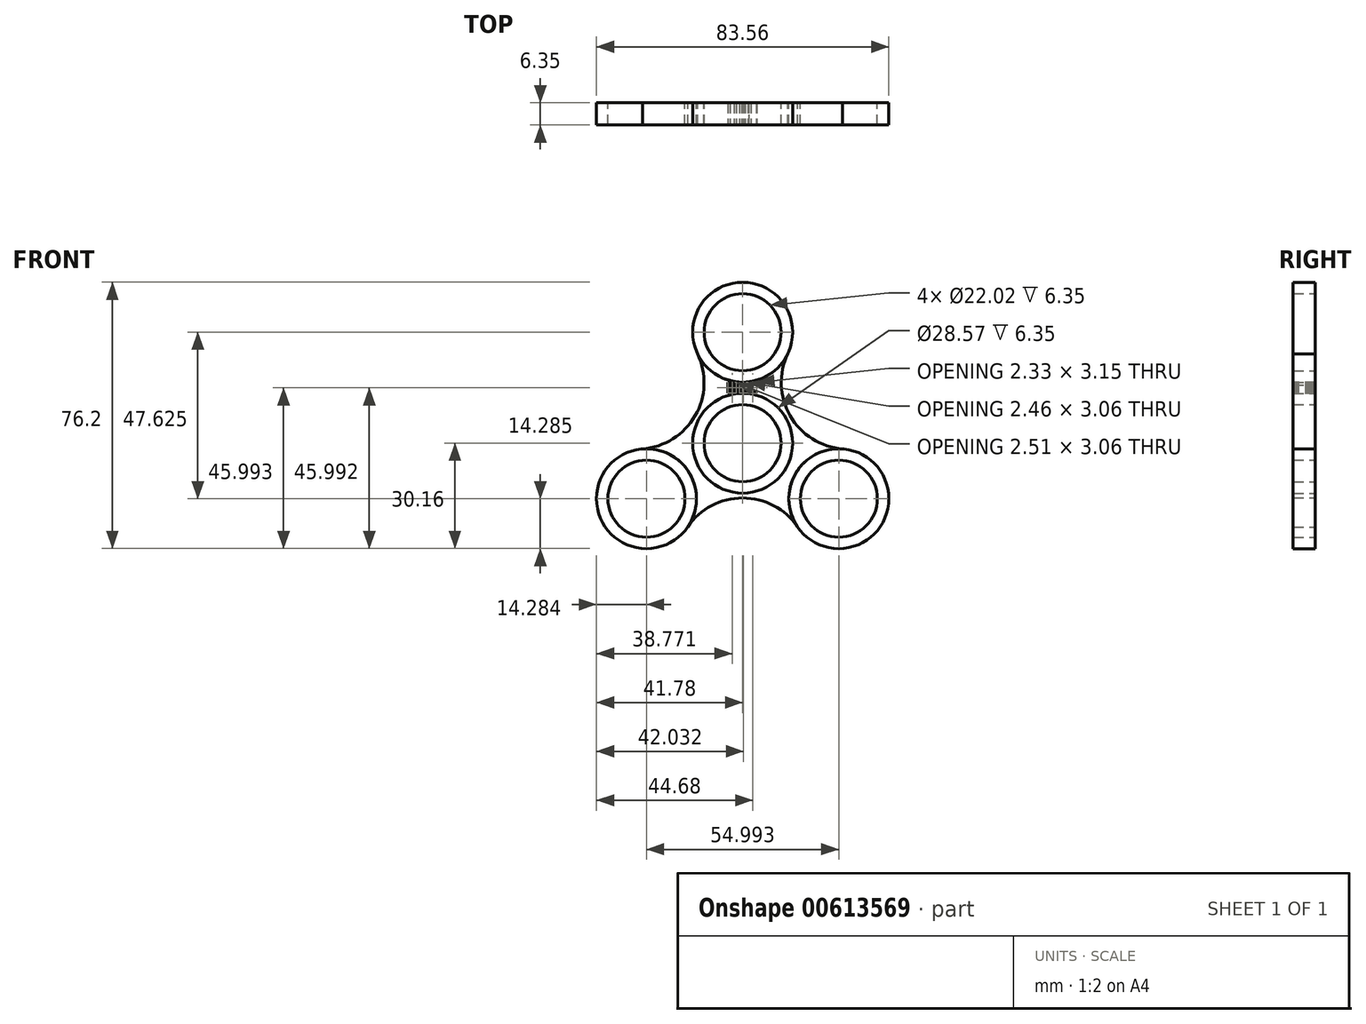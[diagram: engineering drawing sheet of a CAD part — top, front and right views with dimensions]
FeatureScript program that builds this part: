
annotation { "Feature Type Name" : "Feature", "Feature Type Description" : "" }
export const myFeature = defineFeature(function(context is Context, id is Id, definition is map)
    precondition{}
    {
        {
            var Q0;
            Q0=qCreatedBy(makeId("Front.planeOp"),FACE);
            var sketch = newSketch(context, id + "F0", { "sketchPlane" : qUnion([Q0])});
            skCircle(sketch, "E0", {"center": v(0, 0) * mm, "radius": 14.29 * mm});
            skCircle(sketch, "E1", {"center": v(0, 0) * mm, "radius": 11.01 * mm});
            skCircle(sketch, "E2", {"center": v(0, 31.75) * mm, "radius": 14.29 * mm});
            skCircle(sketch, "E3", {"center": v(0, 31.75) * mm, "radius": 11.01 * mm});
            skCircle(sketch, "E4.1.0", {"center": v(-27.5, -15.88) * mm, "radius": 14.29 * mm});
            skCircle(sketch, "E4.1.1", {"center": v(-27.5, -15.88) * mm, "radius": 11.01 * mm});
            skCircle(sketch, "E4.2.0", {"center": v(27.5, -15.88) * mm, "radius": 14.29 * mm});
            skCircle(sketch, "E4.2.1", {"center": v(27.5, -15.88) * mm, "radius": 11.01 * mm});
            skSolve(sketch);
        }
        {
            var Q0;
            Q0=qCreatedBy(makeId("Front.planeOp"),FACE);
            var sketch = newSketch(context, id + "F1", { "sketchPlane" : qUnion([Q0])});
            skCircle(sketch, "E5.0", {"center": v(0, 31.75) * mm, "radius": 11.01 * mm});
            skCircle(sketch, "E6.0", {"center": v(0, 31.75) * mm, "radius": 14.29 * mm});
            skCircle(sketch, "E7.0.0", {"center": v(0, 0) * mm, "radius": 14.29 * mm});
            skCircle(sketch, "E8.0", {"center": v(0, 0) * mm, "radius": 11.01 * mm});
            skCircle(sketch, "E9.0", {"center": v(27.5, -15.88) * mm, "radius": 14.29 * mm});
            skCircle(sketch, "E10.0", {"center": v(27.5, -15.88) * mm, "radius": 11.01 * mm});
            skCircle(sketch, "E11.0", {"center": v(-27.5, -15.88) * mm, "radius": 14.29 * mm});
            skCircle(sketch, "E12.0", {"center": v(-27.5, -15.88) * mm, "radius": 11.01 * mm});
            skArc(sketch, "E13", {"start": v(12.89, 25.58) * mm, "mid": v(13.58, 7.84) * mm, "end": v(28.6, -1.63) * mm});
            skArc(sketch, "E14", {"start": v(15.71, -23.95) * mm, "mid": v(0, -15.68) * mm, "end": v(-15.71, -23.95) * mm});
            skArc(sketch, "E15", {"start": v(-28.6, -1.63) * mm, "mid": v(-13.58, 7.84) * mm, "end": v(-12.89, 25.58) * mm});
            skSolve(sketch);
        }
        {
            var Q0;
            Q0=makeQuery(id+"F0.imprint","IMPRINT",FACE,{"disambiguationData":[TD([[makeQuery(id+"F0.imprint","IMPRINT",EDGE,{"derivedFrom":sQuery(id+"F0.wireOp",EDGE,"E0")}),1.0]])]});
            var Q1;
            {var subQ1=sQuery(id+"F1.wireOp",EDGE,"48TY5wtY-f8Vi-w7Lm-ik54-9AL8dvb25lUl");Q1=makeQuery(id+"F1.imprint","IMPRINT",FACE,{"disambiguationData":[TD([[makeQuery(id+"F1.imprint","IMPRINT",EDGE,{"derivedFrom":subQ1}),-1.0]])]});}
            var Q2;
            Q2=makeQuery(id+"F0.imprint","IMPRINT",FACE,{"disambiguationData":[TD([[makeQuery(id+"F0.imprint","IMPRINT",EDGE,{"derivedFrom":sQuery(id+"F0.wireOp",EDGE,"E2")}),1.0]])]});
            var Q3;
            Q3=makeQuery(id+"F0.imprint","IMPRINT",FACE,{"disambiguationData":[TD([[makeQuery(id+"F0.imprint","IMPRINT",EDGE,{"derivedFrom":sQuery(id+"F0.wireOp",EDGE,"E4.2.0")}),1.0]])]});
            var Q4;
            Q4=makeQuery(id+"F0.imprint","IMPRINT",FACE,{"disambiguationData":[TD([[makeQuery(id+"F0.imprint","IMPRINT",EDGE,{"derivedFrom":sQuery(id+"F0.wireOp",EDGE,"E4.1.0")}),1.0]])]});
            var Q5;
            {var subQ1=sQuery(id+"F1.wireOp",EDGE,"Ib90Gd8R-m9Zh-xETc-l9XS-3snbVAfNY6uZ");Q5=makeQuery(id+"F1.imprint","IMPRINT",FACE,{"disambiguationData":[TD([[makeQuery(id+"F1.imprint","IMPRINT",EDGE,{"derivedFrom":subQ1}),-1.0]])]});}
            var Q6;
            Q6=makeQuery(id+"F1.imprint","IMPRINT",FACE,{"disambiguationData":[TD([[makeQuery(id+"F1.imprint","IMPRINT",EDGE,{"derivedFrom":sQuery(id+"F1.wireOp",EDGE,"E7.0.0")}),-1.0]])]});
            extrude(context, id + "F2", {"entities" : qUnion([Q0, Q1, Q2, Q3, Q4, Q5, Q6]), "depth" : 6.35 * mm, "offsetDistance" : 25.4 * mm});
        }
        {
            var Q0;
            Q0=makeQuery(id+"F2.opExtrude","CAP_FACE",FACE,{"disambiguationData":[OSD([sQuery(id+"F1.wireOp",EDGE,"E6.0"),sQuery(id+"F1.wireOp",EDGE,"E7.0.0"),sQuery(id+"F1.wireOp",EDGE,"E9.0"),sQuery(id+"F1.wireOp",EDGE,"E11.0"),sQuery(id+"F1.wireOp",EDGE,"E13"),sQuery(id+"F1.wireOp",EDGE,"E14"),sQuery(id+"F1.wireOp",EDGE,"E15")])],"isStart":false});
            var sketch = newSketch(context, id + "F3", { "sketchPlane" : qUnion([Q0])});
            skText(sketch, "E16", { "text": "HKC", "fontName": "OpenSans-Bold.ttf"});
            const initialGuessF3  = {"E16": [-0.00465, 0.0143, 1, 0, 0.00309]};
            skSetInitialGuess(sketch, initialGuessF3);
            skSolve(sketch);
        }
        {
            var Q0;
            Q0 = qSketchRegion(id + "F3", true);
            extrude(context, id + "F4", {"entities" : qUnion([Q0]), "operationType" : NewBodyOperationType.REMOVE, "endBound" : BoundingType.THROUGH_ALL, "oppositeDirection" : true, "depth" : 25.4 * mm, "offsetDistance" : 25.4 * mm});
        }
    });
